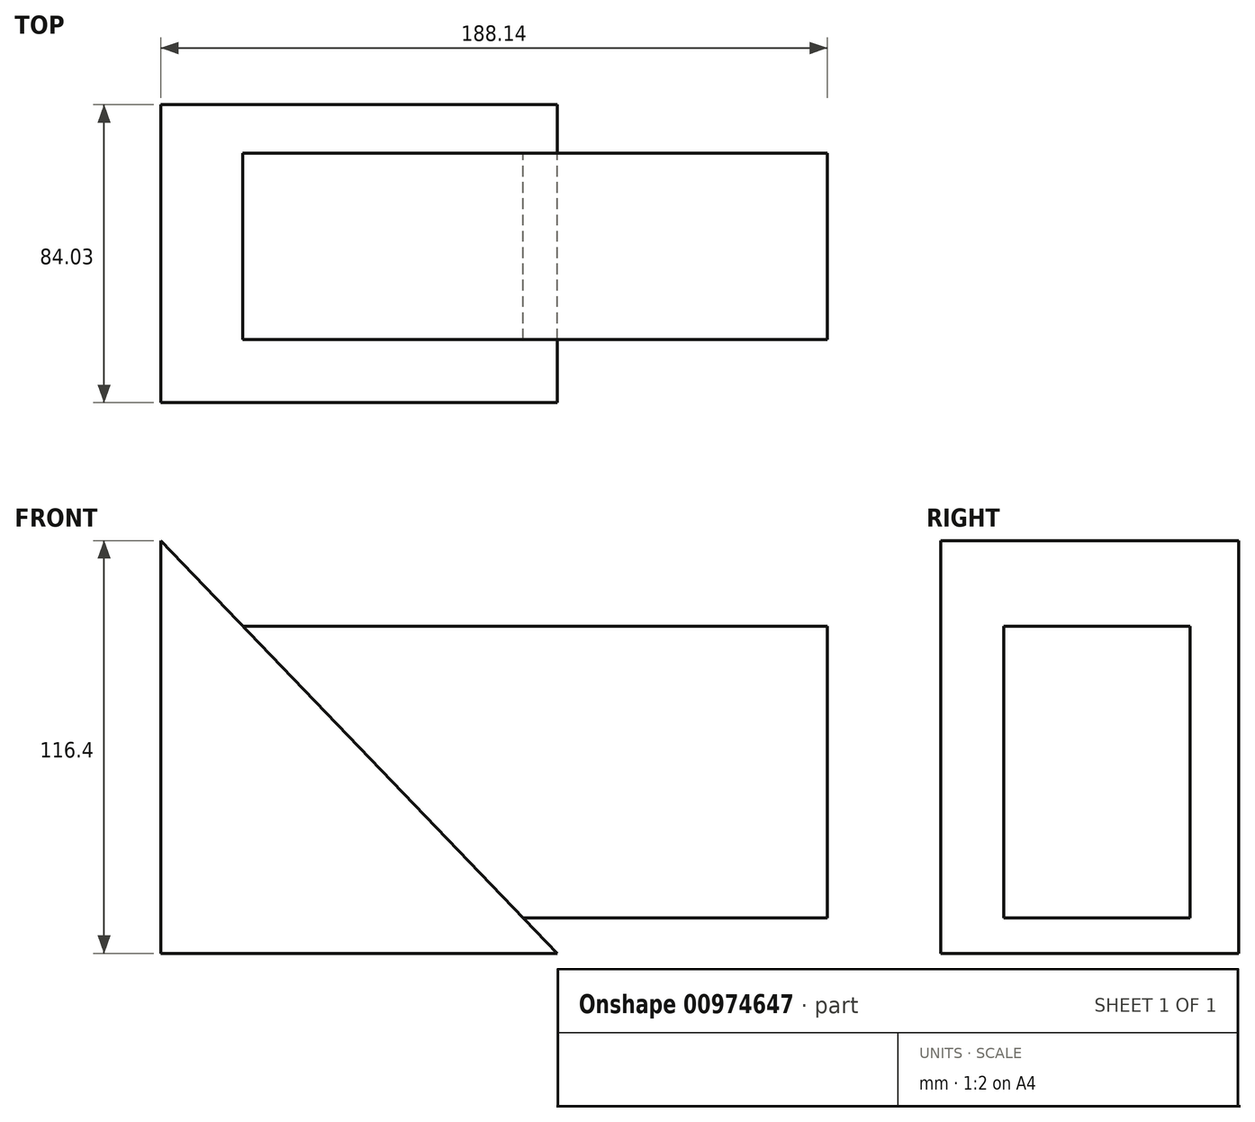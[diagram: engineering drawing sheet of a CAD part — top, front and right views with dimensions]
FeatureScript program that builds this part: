
annotation { "Feature Type Name" : "Feature", "Feature Type Description" : "" }
export const myFeature = defineFeature(function(context is Context, id is Id, definition is map)
    precondition{}
    {
        {
            var Q0;
            Q0=qCreatedBy(makeId("Front.planeOp"),FACE);
            var sketch = newSketch(context, id + "F0", { "sketchPlane" : qUnion([Q0])});
            skLineSegment(sketch, "E0", {"start": v(-53.5, 52.5) * mm, "end": v(-53.5, -63.9) * mm});
            skLineSegment(sketch, "E1", {"start": v(-53.5, -63.9) * mm, "end": v(58.45, -63.9) * mm});
            skLineSegment(sketch, "E2", {"start": v(58.45, -63.9) * mm, "end": v(-53.5, 52.5) * mm});
            skSolve(sketch);
        }
        {
            var Q0;
            Q0=makeQuery(id+"F0.imprint","IMPRINT",FACE,{"disambiguationData":[TD([[makeQuery(id+"F0.imprint","IMPRINT",EDGE,{"derivedFrom":sQuery(id+"F0.wireOp",EDGE,"E0")}),1.0]])]});
            extrude(context, id + "F1", {"entities" : qUnion([Q0]), "depth" : 84.03 * mm, "offsetDistance" : 25.4 * mm});
        }
        {
            var Q0;
            Q0=qCreatedBy(makeId("Right.planeOp"),FACE);
            var sketch = newSketch(context, id + "F2", { "sketchPlane" : qUnion([Q0])});
            skLineSegment(sketch, "E3.bottom", {"start": v(-66.22, 28.4) * mm, "end": v(-13.67, 28.4) * mm});
            skLineSegment(sketch, "E3.top", {"start": v(-66.22, -53.88) * mm, "end": v(-13.67, -53.88) * mm});
            skLineSegment(sketch, "E3.left", {"start": v(-66.22, 28.4) * mm, "end": v(-66.22, -53.88) * mm});
            skLineSegment(sketch, "E3.right", {"start": v(-13.67, 28.4) * mm, "end": v(-13.67, -53.88) * mm});
            skSolve(sketch);
        }
        {
            var Q0;
            Q0=qCreatedBy(makeId("Right.planeOp"),FACE);
            cPlane(context, id + "F3", {"entities" : qUnion([Q0]), "cplaneType" : CPlaneType.OFFSET, "offset" : 134.63 * mm, "width" : 152.4 * mm, "height" : 152.4 * mm});
        }
        {
            var Q0;
            Q0=qCreatedBy(id+"F3.planeOp",FACE);
            var sketch = newSketch(context, id + "F4", { "sketchPlane" : qUnion([Q0])});
            skLineSegment(sketch, "E4.0.0", {"start": v(-66.22, 28.4) * mm, "end": v(-66.22, -53.88) * mm});
            skLineSegment(sketch, "E4.0.1", {"start": v(-66.22, -53.88) * mm, "end": v(-13.67, -53.88) * mm});
            skLineSegment(sketch, "E4.0.2", {"start": v(-13.67, -53.88) * mm, "end": v(-13.67, 28.4) * mm});
            skLineSegment(sketch, "E4.0.3", {"start": v(-13.67, 28.4) * mm, "end": v(-66.22, 28.4) * mm});
            skSolve(sketch);
        }
        {
            var Q0;
            Q0=makeQuery(id+"F4.imprint","IMPRINT",FACE,{"disambiguationData":[TD([[makeQuery(id+"F4.imprint","IMPRINT",EDGE,{"derivedFrom":sQuery(id+"F4.wireOp",EDGE,"E4.0.0")}),1.0]])]});
            var Q1;
            Q1=makeQuery(id+"F1.opExtrude","SWEPT_FACE",FACE,{"disambiguationData":[OSD([sQuery(id+"F0.wireOp",EDGE,"E2")])]});
            extrude(context, id + "F5", {"entities" : qUnion([Q0]), "operationType" : NewBodyOperationType.ADD, "endBound" : BoundingType.UP_TO_SURFACE, "oppositeDirection" : true, "depth" : 25.4 * mm, "endBoundEntityFace" : qUnion([Q1]), "offsetDistance" : 25.4 * mm});
        }
    });
